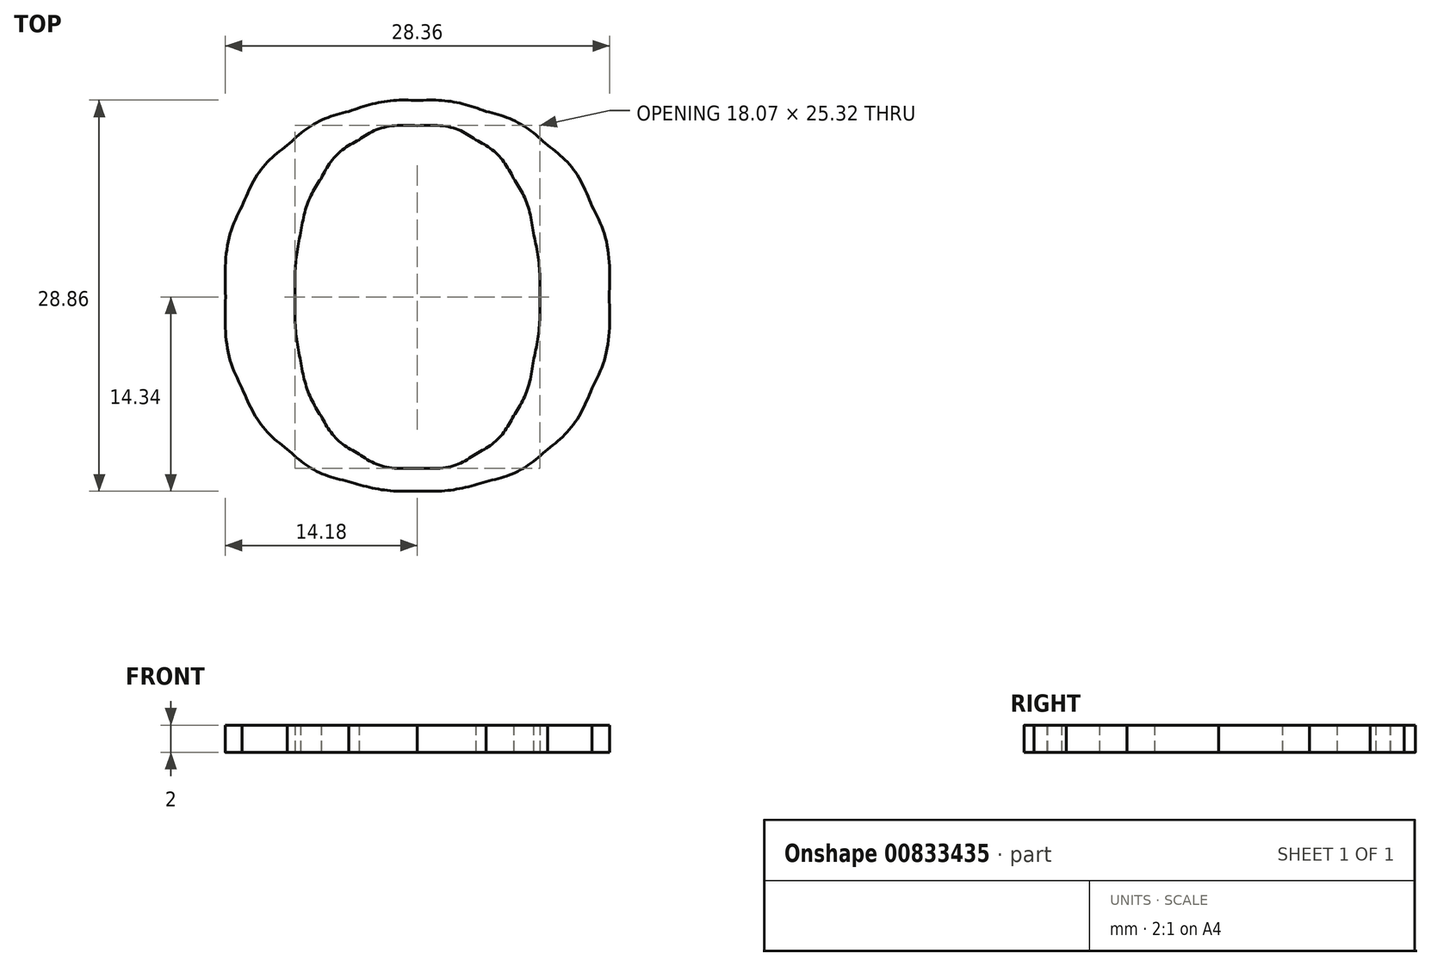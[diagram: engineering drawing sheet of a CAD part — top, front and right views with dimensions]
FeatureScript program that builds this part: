
annotation { "Feature Type Name" : "Feature", "Feature Type Description" : "" }
export const myFeature = defineFeature(function(context is Context, id is Id, definition is map)
    precondition{}
    {
        {
            var Q0;
            Q0=qCreatedBy(makeId("Top.planeOp"),FACE);
            var sketch = newSketch(context, id + "F0", { "sketchPlane" : qUnion([Q0])});
            skLineSegment(sketch, "E0", {"start": v(-37.54, 32.6) * mm, "end": v(-37.54, 22.58) * mm});
            skLineSegment(sketch, "E1", {"start": v(-37.54, 22.58) * mm, "end": v(-37.54, 32.6) * mm});
            skLineSegment(sketch, "E2", {"start": v(-32.77, 18.91) * mm, "end": v(-32.77, 22.4) * mm});
            skLineSegment(sketch, "E3", {"start": v(-32.77, 22.4) * mm, "end": v(-32.77, 24.68) * mm});
            skLineSegment(sketch, "E4", {"start": v(-32.77, 24.68) * mm, "end": v(-32.77, 18.91) * mm});
            skLineSegment(sketch, "E5", {"start": v(-9.25, 34.75) * mm, "end": v(-9.25, 24.21) * mm});
            skLineSegment(sketch, "E6", {"start": v(-9.25, 24.21) * mm, "end": v(-9.25, 34.75) * mm});
            skLineSegment(sketch, "E7", {"start": v(-4.94, 17.7) * mm, "end": v(-4.94, 21.19) * mm});
            skLineSegment(sketch, "E8", {"start": v(-4.94, 21.19) * mm, "end": v(-4.94, 17.7) * mm});
            skLineSegment(sketch, "E9", {"start": v(-4.94, 24.15) * mm, "end": v(-4.94, 34.75) * mm});
            skLineSegment(sketch, "E10", {"start": v(-4.94, 34.75) * mm, "end": v(-4.94, 24.15) * mm});
            skLineSegment(sketch, "E11", {"start": v(-35.72, -38.69) * mm, "end": v(-36.42, -38.69) * mm});
            skLineSegment(sketch, "E12", {"start": v(-36.42, -38.69) * mm, "end": v(-35.72, -38.69) * mm});
            skLineSegment(sketch, "E13", {"start": v(-17.56, -13.13) * mm, "end": v(-16.86, -13.13) * mm});
            skLineSegment(sketch, "E14", {"start": v(-16.86, -13.13) * mm, "end": v(-17.56, -13.13) * mm});
            skLineSegment(sketch, "E15", {"start": v(-7.25, -35.54) * mm, "end": v(-7.25, -44.98) * mm});
            skLineSegment(sketch, "E16", {"start": v(-7.25, -44.98) * mm, "end": v(-7.25, -35.54) * mm});
            skLineSegment(sketch, "E17", {"start": v(-2.94, -44.98) * mm, "end": v(-2.94, -41.3) * mm});
            skLineSegment(sketch, "E18", {"start": v(-2.94, -41.3) * mm, "end": v(-2.83, -41.3) * mm});
            skLineSegment(sketch, "E19", {"start": v(-2.83, -41.3) * mm, "end": v(-2.94, -44.98) * mm});
            skLineSegment(sketch, "E20", {"start": v(-2.83, -24.3) * mm, "end": v(-2.94, -24.3) * mm});
            skLineSegment(sketch, "E21", {"start": v(-2.94, -24.3) * mm, "end": v(-2.83, -24.3) * mm});
            skLineSegment(sketch, "E22", {"start": v(40.76, -31.76) * mm, "end": v(40.53, -40.5) * mm});
            skLineSegment(sketch, "E23", {"start": v(40.53, -40.5) * mm, "end": v(40.76, -31.76) * mm});
            skLineSegment(sketch, "E24", {"start": v(26.38, -21.4) * mm, "end": v(26.38, -24.42) * mm});
            skLineSegment(sketch, "E25", {"start": v(26.38, -24.42) * mm, "end": v(27.02, -24.42) * mm});
            skLineSegment(sketch, "E26", {"start": v(27.02, -24.42) * mm, "end": v(26.38, -21.4) * mm});
            skLineSegment(sketch, "E27", {"start": v(48.45, -45.56) * mm, "end": v(48.45, -44.28) * mm});
            skLineSegment(sketch, "E28", {"start": v(48.45, -44.28) * mm, "end": v(48.45, -45.56) * mm});
            skFitSpline(sketch, "E29", {"points": [v(-37.54, 22.58) * mm, v(-37.54, 20.02) * mm, v(-37.6, 17.5) * mm, v(-37.72, 15.01) * mm]});
            skFitSpline(sketch, "E30", {"points": [v(-37.72, 15.01) * mm, v(-37.8, 12.57) * mm, v(-37.9, 10.1) * mm, v(-38.01, 7.62) * mm]});
            skFitSpline(sketch, "E31", {"points": [v(-38.01, 7.62) * mm, v(-36.23, 7.7) * mm, v(-34.46, 7.74) * mm, v(-32.71, 7.74) * mm]});
            skFitSpline(sketch, "E32", {"points": [v(-32.71, 7.74) * mm, v(-30.97, 7.74) * mm, v(-29.2, 7.74) * mm, v(-27.41, 7.74) * mm]});
            skFitSpline(sketch, "E33", {"points": [v(-27.41, 7.74) * mm, v(-25.63, 7.74) * mm, v(-23.88, 7.74) * mm, v(-22.17, 7.74) * mm]});
            skFitSpline(sketch, "E34", {"points": [v(-22.17, 7.74) * mm, v(-20.43, 7.74) * mm, v(-18.68, 7.7) * mm, v(-16.93, 7.62) * mm]});
            skFitSpline(sketch, "E35", {"points": [v(-16.93, 7.62) * mm, v(-17.05, 8) * mm, v(-17.1, 8.51) * mm, v(-17.1, 9.13) * mm]});
            skFitSpline(sketch, "E36", {"points": [v(-17.1, 9.13) * mm, v(-17.1, 9.4) * mm, v(-17.1, 9.7) * mm, v(-17.1, 10) * mm]});
            skFitSpline(sketch, "E37", {"points": [v(-17.1, 10) * mm, v(-17.07, 10.36) * mm, v(-17.01, 10.67) * mm, v(-16.93, 10.94) * mm]});
            skFitSpline(sketch, "E38", {"points": [v(-16.93, 10.94) * mm, v(-17.87, 10.74) * mm, v(-18.97, 10.59) * mm, v(-20.25, 10.47) * mm]});
            skFitSpline(sketch, "E39", {"points": [v(-20.25, 10.47) * mm, v(-21.5, 10.4) * mm, v(-22.83, 10.32) * mm, v(-24.27, 10.24) * mm]});
            skFitSpline(sketch, "E40", {"points": [v(-24.27, 10.24) * mm, v(-25.67, 10.2) * mm, v(-27.1, 10.18) * mm, v(-28.58, 10.18) * mm]});
            skFitSpline(sketch, "E41", {"points": [v(-28.58, 10.18) * mm, v(-30.01, 10.18) * mm, v(-31.37, 10.18) * mm, v(-32.65, 10.18) * mm]});
            skFitSpline(sketch, "E42", {"points": [v(-32.65, 10.18) * mm, v(-32.7, 10.92) * mm, v(-32.73, 12) * mm, v(-32.77, 13.44) * mm]});
            skFitSpline(sketch, "E43", {"points": [v(-32.77, 13.44) * mm, v(-32.77, 14.88) * mm, v(-32.77, 16.7) * mm, v(-32.77, 18.91) * mm]});
            skFitSpline(sketch, "E44", {"points": [v(-32.77, 24.68) * mm, v(-32.77, 25.3) * mm, v(-32.77, 25.8) * mm, v(-32.77, 26.2) * mm]});
            skFitSpline(sketch, "E45", {"points": [v(-32.77, 26.2) * mm, v(-32.73, 26.62) * mm, v(-32.71, 27) * mm, v(-32.71, 27.36) * mm]});
            skFitSpline(sketch, "E46", {"points": [v(-32.71, 27.36) * mm, v(-32.01, 27.36) * mm, v(-31.08, 27.34) * mm, v(-29.92, 27.3) * mm]});
            skFitSpline(sketch, "E47", {"points": [v(-29.92, 27.3) * mm, v(-28.71, 27.3) * mm, v(-27.45, 27.28) * mm, v(-26.13, 27.24) * mm]});
            skFitSpline(sketch, "E48", {"points": [v(-26.13, 27.24) * mm, v(-24.77, 27.24) * mm, v(-23.44, 27.2) * mm, v(-22.12, 27.12) * mm]});
            skFitSpline(sketch, "E49", {"points": [v(-22.12, 27.12) * mm, v(-20.76, 27.05) * mm, v(-19.57, 26.95) * mm, v(-18.56, 26.83) * mm]});
            skFitSpline(sketch, "E50", {"points": [v(-18.56, 26.83) * mm, v(-18.68, 27.42) * mm, v(-18.74, 28) * mm, v(-18.74, 28.58) * mm]});
            skFitSpline(sketch, "E51", {"points": [v(-18.74, 28.58) * mm, v(-18.74, 29.2) * mm, v(-18.68, 29.8) * mm, v(-18.56, 30.38) * mm]});
            skFitSpline(sketch, "E52", {"points": [v(-18.56, 30.38) * mm, v(-19.42, 30.3) * mm, v(-20.33, 30.23) * mm, v(-21.3, 30.15) * mm]});
            skFitSpline(sketch, "E53", {"points": [v(-21.3, 30.15) * mm, v(-22.23, 30.11) * mm, v(-23.26, 30.06) * mm, v(-24.39, 29.98) * mm]});
            skFitSpline(sketch, "E54", {"points": [v(-24.39, 29.98) * mm, v(-25.51, 29.94) * mm, v(-26.75, 29.9) * mm, v(-28.11, 29.86) * mm]});
            skFitSpline(sketch, "E55", {"points": [v(-28.11, 29.86) * mm, v(-29.47, 29.82) * mm, v(-31, 29.8) * mm, v(-32.71, 29.8) * mm]});
            skFitSpline(sketch, "E56", {"points": [v(-32.71, 29.8) * mm, v(-32.71, 30.54) * mm, v(-32.73, 31.63) * mm, v(-32.77, 33.06) * mm]});
            skFitSpline(sketch, "E57", {"points": [v(-32.77, 33.06) * mm, v(-32.77, 34.5) * mm, v(-32.77, 35.97) * mm, v(-32.77, 37.49) * mm]});
            skFitSpline(sketch, "E58", {"points": [v(-32.77, 37.49) * mm, v(-32.77, 38.92) * mm, v(-32.75, 40.2) * mm, v(-32.71, 41.33) * mm]});
            skFitSpline(sketch, "E59", {"points": [v(-32.71, 41.33) * mm, v(-32.63, 42.46) * mm, v(-32.58, 43.64) * mm, v(-32.54, 44.88) * mm]});
            skFitSpline(sketch, "E60", {"points": [v(-32.54, 44.88) * mm, v(-30.64, 44.88) * mm, v(-29, 44.84) * mm, v(-27.65, 44.77) * mm]});
            skFitSpline(sketch, "E61", {"points": [v(-27.65, 44.77) * mm, v(-26.29, 44.73) * mm, v(-25.05, 44.67) * mm, v(-23.92, 44.6) * mm]});
            skFitSpline(sketch, "E62", {"points": [v(-23.92, 44.6) * mm, v(-22.76, 44.51) * mm, v(-21.67, 44.44) * mm, v(-20.66, 44.36) * mm]});
            skFitSpline(sketch, "E63", {"points": [v(-20.66, 44.36) * mm, v(-19.61, 44.28) * mm, v(-18.47, 44.2) * mm, v(-17.22, 44.13) * mm]});
            skFitSpline(sketch, "E64", {"points": [v(-17.22, 44.13) * mm, v(-17.34, 44.7) * mm, v(-17.4, 45.3) * mm, v(-17.4, 45.87) * mm]});
            skFitSpline(sketch, "E65", {"points": [v(-17.4, 45.87) * mm, v(-17.4, 46.45) * mm, v(-17.34, 47.04) * mm, v(-17.22, 47.62) * mm]});
            skFitSpline(sketch, "E66", {"points": [v(-17.22, 47.62) * mm, v(-18.97, 47.54) * mm, v(-20.7, 47.46) * mm, v(-22.4, 47.39) * mm]});
            skFitSpline(sketch, "E67", {"points": [v(-22.4, 47.39) * mm, v(-24.11, 47.35) * mm, v(-25.84, 47.33) * mm, v(-27.59, 47.33) * mm]});
            skFitSpline(sketch, "E68", {"points": [v(-27.59, 47.33) * mm, v(-29.34, 47.33) * mm, v(-31.08, 47.35) * mm, v(-32.83, 47.39) * mm]});
            skFitSpline(sketch, "E69", {"points": [v(-32.83, 47.39) * mm, v(-34.54, 47.46) * mm, v(-36.26, 47.54) * mm, v(-38.01, 47.62) * mm]});
            skFitSpline(sketch, "E70", {"points": [v(-38.01, 47.62) * mm, v(-37.9, 45.14) * mm, v(-37.8, 42.65) * mm, v(-37.72, 40.17) * mm]});
            skFitSpline(sketch, "E71", {"points": [v(-37.72, 40.17) * mm, v(-37.6, 37.68) * mm, v(-37.54, 35.16) * mm, v(-37.54, 32.6) * mm]});
            skFitSpline(sketch, "E72", {"points": [v(-9.25, 24.21) * mm, v(-9.25, 22.9) * mm, v(-9.27, 21.46) * mm, v(-9.3, 19.9) * mm]});
            skFitSpline(sketch, "E73", {"points": [v(-9.3, 19.9) * mm, v(-9.3, 18.35) * mm, v(-9.33, 16.82) * mm, v(-9.36, 15.3) * mm]});
            skFitSpline(sketch, "E74", {"points": [v(-9.36, 15.3) * mm, v(-9.4, 13.8) * mm, v(-9.46, 12.35) * mm, v(-9.54, 11) * mm]});
            skFitSpline(sketch, "E75", {"points": [v(-9.54, 11) * mm, v(-9.58, 9.64) * mm, v(-9.64, 8.51) * mm, v(-9.71, 7.62) * mm]});
            skFitSpline(sketch, "E76", {"points": [v(-9.71, 7.62) * mm, v(-8.82, 7.7) * mm, v(-7.95, 7.74) * mm, v(-7.1, 7.74) * mm]});
            skFitSpline(sketch, "E77", {"points": [v(-7.1, 7.74) * mm, v(-6.24, 7.74) * mm, v(-5.37, 7.7) * mm, v(-4.47, 7.62) * mm]});
            skFitSpline(sketch, "E78", {"points": [v(-4.47, 7.62) * mm, v(-4.67, 9.29) * mm, v(-4.8, 10.94) * mm, v(-4.88, 12.57) * mm]});
            skFitSpline(sketch, "E79", {"points": [v(-4.88, 12.57) * mm, v(-4.92, 14.24) * mm, v(-4.94, 15.95) * mm, v(-4.94, 17.7) * mm]});
            skFitSpline(sketch, "E80", {"points": [v(-4.94, 21.19) * mm, v(-4.94, 21.65) * mm, v(-4.75, 21.88) * mm, v(-4.36, 21.88) * mm]});
            skFitSpline(sketch, "E81", {"points": [v(-4.36, 21.88) * mm, v(-4.2, 21.88) * mm, v(-4.05, 21.83) * mm, v(-3.9, 21.7) * mm]});
            skFitSpline(sketch, "E82", {"points": [v(-3.9, 21.7) * mm, v(-3.74, 21.6) * mm, v(-3.6, 21.46) * mm, v(-3.48, 21.3) * mm]});
            skFitSpline(sketch, "E83", {"points": [v(-3.48, 21.3) * mm, v(-2.79, 20.56) * mm, v(-1.95, 19.63) * mm, v(-0.98, 18.5) * mm]});
            skFitSpline(sketch, "E84", {"points": [v(-0.98, 18.5) * mm, v(0, 17.38) * mm, v(1, 16.18) * mm, v(2.05, 14.9) * mm]});
            skFitSpline(sketch, "E85", {"points": [v(2.05, 14.9) * mm, v(3.13, 13.62) * mm, v(4.22, 12.32) * mm, v(5.3, 11) * mm]});
            skFitSpline(sketch, "E86", {"points": [v(5.3, 11) * mm, v(6.4, 9.72) * mm, v(7.37, 8.59) * mm, v(8.22, 7.62) * mm]});
            skFitSpline(sketch, "E87", {"points": [v(8.22, 7.62) * mm, v(8.76, 7.7) * mm, v(9.29, 7.74) * mm, v(9.8, 7.74) * mm]});
            skFitSpline(sketch, "E88", {"points": [v(9.8, 7.74) * mm, v(10.3, 7.74) * mm, v(10.76, 7.74) * mm, v(11.19, 7.74) * mm]});
            skFitSpline(sketch, "E89", {"points": [v(11.19, 7.74) * mm, v(11.7, 7.74) * mm, v(12.2, 7.74) * mm, v(12.7, 7.74) * mm]});
            skFitSpline(sketch, "E90", {"points": [v(12.7, 7.74) * mm, v(13.25, 7.74) * mm, v(13.85, 7.7) * mm, v(14.5, 7.62) * mm]});
            skFitSpline(sketch, "E91", {"points": [v(14.5, 7.62) * mm, v(12.06, 10.22) * mm, v(9.66, 12.86) * mm, v(7.29, 15.54) * mm]});
            skFitSpline(sketch, "E92", {"points": [v(7.29, 15.54) * mm, v(4.96, 18.22) * mm, v(2.69, 20.9) * mm, v(0.48, 23.57) * mm]});
            skFitSpline(sketch, "E93", {"points": [v(0.48, 23.57) * mm, v(2.5, 25.55) * mm, v(4.6, 27.5) * mm, v(6.82, 29.4) * mm]});
            skFitSpline(sketch, "E94", {"points": [v(6.82, 29.4) * mm, v(9.07, 31.34) * mm, v(11.42, 33.3) * mm, v(13.87, 35.28) * mm]});
            skFitSpline(sketch, "E95", {"points": [v(13.87, 35.28) * mm, v(13.2, 35.2) * mm, v(12.66, 35.12) * mm, v(12.24, 35.04) * mm]});
            skFitSpline(sketch, "E96", {"points": [v(12.24, 35.04) * mm, v(11.8, 35) * mm, v(11.38, 34.98) * mm, v(10.96, 34.98) * mm]});
            skFitSpline(sketch, "E97", {"points": [v(10.96, 34.98) * mm, v(10.26, 34.98) * mm, v(9.52, 35.08) * mm, v(8.74, 35.28) * mm]});
            skFitSpline(sketch, "E98", {"points": [v(8.74, 35.28) * mm, v(7.85, 34.23) * mm, v(6.86, 33.12) * mm, v(5.77, 31.96) * mm]});
            skFitSpline(sketch, "E99", {"points": [v(5.77, 31.96) * mm, v(4.69, 30.8) * mm, v(3.62, 29.69) * mm, v(2.57, 28.64) * mm]});
            skFitSpline(sketch, "E100", {"points": [v(2.57, 28.64) * mm, v(1.56, 27.63) * mm, v(0.63, 26.74) * mm, v(-0.22, 25.96) * mm]});
            skFitSpline(sketch, "E101", {"points": [v(-0.22, 25.96) * mm, v(-1.04, 25.18) * mm, v(-1.62, 24.66) * mm, v(-1.97, 24.39) * mm]});
            skFitSpline(sketch, "E102", {"points": [v(-1.97, 24.39) * mm, v(-2.44, 24.04) * mm, v(-2.86, 23.73) * mm, v(-3.25, 23.46) * mm]});
            skFitSpline(sketch, "E103", {"points": [v(-3.25, 23.46) * mm, v(-3.6, 23.18) * mm, v(-3.93, 23.05) * mm, v(-4.24, 23.05) * mm]});
            skFitSpline(sketch, "E104", {"points": [v(-4.24, 23.05) * mm, v(-4.7, 23.05) * mm, v(-4.94, 23.42) * mm, v(-4.94, 24.15) * mm]});
            skFitSpline(sketch, "E105", {"points": [v(-4.94, 34.75) * mm, v(-4.94, 36.07) * mm, v(-4.94, 37.5) * mm, v(-4.94, 39.06) * mm]});
            skFitSpline(sketch, "E106", {"points": [v(-4.94, 39.06) * mm, v(-4.9, 40.61) * mm, v(-4.86, 42.15) * mm, v(-4.82, 43.66) * mm]});
            skFitSpline(sketch, "E107", {"points": [v(-4.82, 43.66) * mm, v(-4.78, 45.17) * mm, v(-4.75, 46.61) * mm, v(-4.7, 47.97) * mm]});
            skFitSpline(sketch, "E108", {"points": [v(-4.7, 47.97) * mm, v(-4.63, 49.37) * mm, v(-4.55, 50.55) * mm, v(-4.47, 51.52) * mm]});
            skFitSpline(sketch, "E109", {"points": [v(-4.47, 51.52) * mm, v(-5.56, 51.33) * mm, v(-6.43, 51.23) * mm, v(-7.1, 51.23) * mm]});
            skFitSpline(sketch, "E110", {"points": [v(-7.1, 51.23) * mm, v(-7.75, 51.23) * mm, v(-8.63, 51.33) * mm, v(-9.71, 51.52) * mm]});
            skFitSpline(sketch, "E111", {"points": [v(-9.71, 51.52) * mm, v(-9.64, 50.55) * mm, v(-9.58, 49.37) * mm, v(-9.54, 47.97) * mm]});
            skFitSpline(sketch, "E112", {"points": [v(-9.54, 47.97) * mm, v(-9.46, 46.61) * mm, v(-9.4, 45.17) * mm, v(-9.36, 43.66) * mm]});
            skFitSpline(sketch, "E113", {"points": [v(-9.36, 43.66) * mm, v(-9.33, 42.15) * mm, v(-9.3, 40.61) * mm, v(-9.3, 39.06) * mm]});
            skFitSpline(sketch, "E114", {"points": [v(-9.3, 39.06) * mm, v(-9.27, 37.5) * mm, v(-9.25, 36.07) * mm, v(-9.25, 34.75) * mm]});
            skFitSpline(sketch, "E115", {"points": [v(22.13, 21.36) * mm, v(22.13, 23) * mm, v(22.27, 24.56) * mm, v(22.54, 26.08) * mm]});
            skFitSpline(sketch, "E116", {"points": [v(22.54, 26.08) * mm, v(22.85, 27.6) * mm, v(23.36, 28.93) * mm, v(24.06, 30.1) * mm]});
            skFitSpline(sketch, "E117", {"points": [v(24.06, 30.1) * mm, v(24.75, 31.3) * mm, v(25.69, 32.25) * mm, v(26.85, 32.95) * mm]});
            skFitSpline(sketch, "E118", {"points": [v(26.85, 32.95) * mm, v(28.02, 33.65) * mm, v(29.45, 34) * mm, v(31.16, 34) * mm]});
            skFitSpline(sketch, "E119", {"points": [v(31.16, 34) * mm, v(32.87, 34) * mm, v(34.3, 33.65) * mm, v(35.47, 32.95) * mm]});
            skFitSpline(sketch, "E120", {"points": [v(35.47, 32.95) * mm, v(36.63, 32.25) * mm, v(37.56, 31.3) * mm, v(38.26, 30.1) * mm]});
            skFitSpline(sketch, "E121", {"points": [v(38.26, 30.1) * mm, v(38.96, 28.93) * mm, v(39.45, 27.6) * mm, v(39.72, 26.08) * mm]});
            skFitSpline(sketch, "E122", {"points": [v(39.72, 26.08) * mm, v(40.03, 24.56) * mm, v(40.18, 23) * mm, v(40.18, 21.36) * mm]});
            skFitSpline(sketch, "E123", {"points": [v(40.18, 21.36) * mm, v(40.18, 19.73) * mm, v(40.03, 18.16) * mm, v(39.72, 16.64) * mm]});
            skFitSpline(sketch, "E124", {"points": [v(39.72, 16.64) * mm, v(39.45, 15.13) * mm, v(38.96, 13.77) * mm, v(38.26, 12.57) * mm]});
            skFitSpline(sketch, "E125", {"points": [v(38.26, 12.57) * mm, v(37.56, 11.4) * mm, v(36.63, 10.47) * mm, v(35.47, 9.77) * mm]});
            skFitSpline(sketch, "E126", {"points": [v(35.47, 9.77) * mm, v(34.3, 9.07) * mm, v(32.87, 8.73) * mm, v(31.16, 8.73) * mm]});
            skFitSpline(sketch, "E127", {"points": [v(31.16, 8.73) * mm, v(29.45, 8.73) * mm, v(28.02, 9.07) * mm, v(26.85, 9.77) * mm]});
            skFitSpline(sketch, "E128", {"points": [v(26.85, 9.77) * mm, v(25.69, 10.47) * mm, v(24.75, 11.4) * mm, v(24.06, 12.57) * mm]});
            skFitSpline(sketch, "E129", {"points": [v(24.06, 12.57) * mm, v(23.36, 13.77) * mm, v(22.85, 15.13) * mm, v(22.54, 16.64) * mm]});
            skFitSpline(sketch, "E130", {"points": [v(22.54, 16.64) * mm, v(22.27, 18.16) * mm, v(22.13, 19.73) * mm, v(22.13, 21.36) * mm]});
            skFitSpline(sketch, "E131", {"points": [v(17.01, 21.36) * mm, v(17.01, 18.72) * mm, v(17.42, 16.47) * mm, v(18.23, 14.6) * mm]});
            skFitSpline(sketch, "E132", {"points": [v(18.23, 14.6) * mm, v(19.09, 12.78) * mm, v(20.2, 11.29) * mm, v(21.55, 10.12) * mm]});
            skFitSpline(sketch, "E133", {"points": [v(21.55, 10.12) * mm, v(22.91, 9) * mm, v(24.43, 8.2) * mm, v(26.1, 7.74) * mm]});
            skFitSpline(sketch, "E134", {"points": [v(26.1, 7.74) * mm, v(27.8, 7.27) * mm, v(29.5, 7.04) * mm, v(31.16, 7.04) * mm]});
            skFitSpline(sketch, "E135", {"points": [v(31.16, 7.04) * mm, v(32.87, 7.04) * mm, v(34.56, 7.27) * mm, v(36.23, 7.74) * mm]});
            skFitSpline(sketch, "E136", {"points": [v(36.23, 7.74) * mm, v(37.9, 8.2) * mm, v(39.4, 9) * mm, v(40.77, 10.12) * mm]});
            skFitSpline(sketch, "E137", {"points": [v(40.77, 10.12) * mm, v(42.13, 11.29) * mm, v(43.21, 12.78) * mm, v(44.03, 14.6) * mm]});
            skFitSpline(sketch, "E138", {"points": [v(44.03, 14.6) * mm, v(44.88, 16.47) * mm, v(45.3, 18.72) * mm, v(45.3, 21.36) * mm]});
            skFitSpline(sketch, "E139", {"points": [v(45.3, 21.36) * mm, v(45.3, 24) * mm, v(44.88, 26.23) * mm, v(44.03, 28.06) * mm]});
            skFitSpline(sketch, "E140", {"points": [v(44.03, 28.06) * mm, v(43.21, 29.92) * mm, v(42.13, 31.41) * mm, v(40.77, 32.54) * mm]});
            skFitSpline(sketch, "E141", {"points": [v(40.77, 32.54) * mm, v(39.4, 33.7) * mm, v(37.9, 34.54) * mm, v(36.23, 35.04) * mm]});
            skFitSpline(sketch, "E142", {"points": [v(36.23, 35.04) * mm, v(34.56, 35.59) * mm, v(32.87, 35.86) * mm, v(31.16, 35.86) * mm]});
            skFitSpline(sketch, "E143", {"points": [v(31.16, 35.86) * mm, v(29.5, 35.86) * mm, v(27.8, 35.59) * mm, v(26.1, 35.04) * mm]});
            skFitSpline(sketch, "E144", {"points": [v(26.1, 35.04) * mm, v(24.43, 34.54) * mm, v(22.91, 33.7) * mm, v(21.55, 32.54) * mm]});
            skFitSpline(sketch, "E145", {"points": [v(21.55, 32.54) * mm, v(20.2, 31.41) * mm, v(19.09, 29.92) * mm, v(18.23, 28.06) * mm]});
            skFitSpline(sketch, "E146", {"points": [v(18.23, 28.06) * mm, v(17.42, 26.23) * mm, v(17.01, 24) * mm, v(17.01, 21.36) * mm]});
            skFitSpline(sketch, "E147", {"points": [v(-36.42, -38.69) * mm, v(-36.54, -39.81) * mm, v(-36.67, -40.75) * mm, v(-36.83, -41.48) * mm]});
            skFitSpline(sketch, "E148", {"points": [v(-36.83, -41.48) * mm, v(-36.95, -42.18) * mm, v(-37.18, -42.98) * mm, v(-37.53, -43.87) * mm]});
            skFitSpline(sketch, "E149", {"points": [v(-37.53, -43.87) * mm, v(-36.52, -44.69) * mm, v(-35.28, -45.42) * mm, v(-33.8, -46.08) * mm]});
            skFitSpline(sketch, "E150", {"points": [v(-33.8, -46.08) * mm, v(-32.29, -46.7) * mm, v(-30.33, -47.01) * mm, v(-27.92, -47.01) * mm]});
            skFitSpline(sketch, "E151", {"points": [v(-27.92, -47.01) * mm, v(-25.67, -47.01) * mm, v(-23.67, -46.7) * mm, v(-21.92, -46.08) * mm]});
            skFitSpline(sketch, "E152", {"points": [v(-21.92, -46.08) * mm, v(-20.14, -45.42) * mm, v(-18.64, -44.51) * mm, v(-17.44, -43.35) * mm]});
            skFitSpline(sketch, "E153", {"points": [v(-17.44, -43.35) * mm, v(-16.2, -42.14) * mm, v(-15.27, -40.75) * mm, v(-14.65, -39.15) * mm]});
            skFitSpline(sketch, "E154", {"points": [v(-14.65, -39.15) * mm, v(-13.99, -37.56) * mm, v(-13.66, -35.87) * mm, v(-13.66, -34.09) * mm]});
            skFitSpline(sketch, "E155", {"points": [v(-13.66, -34.09) * mm, v(-13.66, -31.95) * mm, v(-14.12, -30.25) * mm, v(-15.05, -28.97) * mm]});
            skFitSpline(sketch, "E156", {"points": [v(-15.05, -28.97) * mm, v(-15.95, -27.68) * mm, v(-17.07, -26.64) * mm, v(-18.43, -25.82) * mm]});
            skFitSpline(sketch, "E157", {"points": [v(-18.43, -25.82) * mm, v(-19.79, -25) * mm, v(-21.26, -24.33) * mm, v(-22.86, -23.78) * mm]});
            skFitSpline(sketch, "E158", {"points": [v(-22.86, -23.78) * mm, v(-24.4, -23.2) * mm, v(-25.86, -22.56) * mm, v(-27.22, -21.86) * mm]});
            skFitSpline(sketch, "E159", {"points": [v(-27.22, -21.86) * mm, v(-28.58, -21.12) * mm, v(-29.73, -20.23) * mm, v(-30.66, -19.18) * mm]});
            skFitSpline(sketch, "E160", {"points": [v(-30.66, -19.18) * mm, v(-31.55, -18.14) * mm, v(-32, -16.7) * mm, v(-32, -14.88) * mm]});
            skFitSpline(sketch, "E161", {"points": [v(-32, -14.88) * mm, v(-32, -13.83) * mm, v(-31.82, -12.86) * mm, v(-31.47, -11.96) * mm]});
            skFitSpline(sketch, "E162", {"points": [v(-31.47, -11.96) * mm, v(-31.08, -11.07) * mm, v(-30.56, -10.31) * mm, v(-29.9, -9.7) * mm]});
            skFitSpline(sketch, "E163", {"points": [v(-29.9, -9.7) * mm, v(-29.2, -9.03) * mm, v(-28.4, -8.53) * mm, v(-27.51, -8.18) * mm]});
            skFitSpline(sketch, "E164", {"points": [v(-27.51, -8.18) * mm, v(-26.58, -7.83) * mm, v(-25.57, -7.66) * mm, v(-24.49, -7.66) * mm]});
            skFitSpline(sketch, "E165", {"points": [v(-24.49, -7.66) * mm, v(-23.4, -7.66) * mm, v(-22.47, -7.85) * mm, v(-21.7, -8.24) * mm]});
            skFitSpline(sketch, "E166", {"points": [v(-21.7, -8.24) * mm, v(-20.91, -8.59) * mm, v(-20.25, -9.03) * mm, v(-19.71, -9.58) * mm]});
            skFitSpline(sketch, "E167", {"points": [v(-19.71, -9.58) * mm, v(-19.13, -10.12) * mm, v(-18.68, -10.72) * mm, v(-18.37, -11.38) * mm]});
            skFitSpline(sketch, "E168", {"points": [v(-18.37, -11.38) * mm, v(-18.02, -12) * mm, v(-17.75, -12.59) * mm, v(-17.56, -13.13) * mm]});
            skFitSpline(sketch, "E169", {"points": [v(-16.86, -13.13) * mm, v(-16.63, -12) * mm, v(-16.4, -11.07) * mm, v(-16.16, -10.33) * mm]});
            skFitSpline(sketch, "E170", {"points": [v(-16.16, -10.33) * mm, v(-15.93, -9.6) * mm, v(-15.64, -8.9) * mm, v(-15.29, -8.24) * mm]});
            skFitSpline(sketch, "E171", {"points": [v(-15.29, -8.24) * mm, v(-16.45, -7.3) * mm, v(-17.71, -6.63) * mm, v(-19.07, -6.2) * mm]});
            skFitSpline(sketch, "E172", {"points": [v(-19.07, -6.2) * mm, v(-20.43, -5.73) * mm, v(-22.04, -5.5) * mm, v(-23.9, -5.5) * mm]});
            skFitSpline(sketch, "E173", {"points": [v(-23.9, -5.5) * mm, v(-25.84, -5.5) * mm, v(-27.6, -5.77) * mm, v(-29.14, -6.32) * mm]});
            skFitSpline(sketch, "E174", {"points": [v(-29.14, -6.32) * mm, v(-30.7, -6.86) * mm, v(-32.04, -7.62) * mm, v(-33.16, -8.59) * mm]});
            skFitSpline(sketch, "E175", {"points": [v(-33.16, -8.59) * mm, v(-34.25, -9.56) * mm, v(-35.08, -10.72) * mm, v(-35.66, -12.08) * mm]});
            skFitSpline(sketch, "E176", {"points": [v(-35.66, -12.08) * mm, v(-36.25, -13.4) * mm, v(-36.54, -14.88) * mm, v(-36.54, -16.5) * mm]});
            skFitSpline(sketch, "E177", {"points": [v(-36.54, -16.5) * mm, v(-36.54, -18.8) * mm, v(-36.1, -20.62) * mm, v(-35.2, -21.98) * mm]});
            skFitSpline(sketch, "E178", {"points": [v(-35.2, -21.98) * mm, v(-34.27, -23.34) * mm, v(-33.12, -24.46) * mm, v(-31.76, -25.36) * mm]});
            skFitSpline(sketch, "E179", {"points": [v(-31.76, -25.36) * mm, v(-30.4, -26.2) * mm, v(-28.95, -26.93) * mm, v(-27.4, -27.5) * mm]});
            skFitSpline(sketch, "E180", {"points": [v(-27.4, -27.5) * mm, v(-25.8, -28.1) * mm, v(-24.33, -28.73) * mm, v(-22.97, -29.43) * mm]});
            skFitSpline(sketch, "E181", {"points": [v(-22.97, -29.43) * mm, v(-21.61, -30.13) * mm, v(-20.49, -31) * mm, v(-19.6, -32.05) * mm]});
            skFitSpline(sketch, "E182", {"points": [v(-19.6, -32.05) * mm, v(-18.66, -33.1) * mm, v(-18.2, -34.52) * mm, v(-18.2, -36.3) * mm]});
            skFitSpline(sketch, "E183", {"points": [v(-18.2, -36.3) * mm, v(-18.2, -37.47) * mm, v(-18.4, -38.57) * mm, v(-18.78, -39.62) * mm]});
            skFitSpline(sketch, "E184", {"points": [v(-18.78, -39.62) * mm, v(-19.17, -40.63) * mm, v(-19.73, -41.52) * mm, v(-20.47, -42.3) * mm]});
            skFitSpline(sketch, "E185", {"points": [v(-20.47, -42.3) * mm, v(-21.17, -43.04) * mm, v(-22.04, -43.64) * mm, v(-23.09, -44.1) * mm]});
            skFitSpline(sketch, "E186", {"points": [v(-23.09, -44.1) * mm, v(-24.1, -44.53) * mm, v(-25.24, -44.74) * mm, v(-26.52, -44.74) * mm]});
            skFitSpline(sketch, "E187", {"points": [v(-26.52, -44.74) * mm, v(-27.77, -44.74) * mm, v(-28.9, -44.57) * mm, v(-29.9, -44.22) * mm]});
            skFitSpline(sketch, "E188", {"points": [v(-29.9, -44.22) * mm, v(-30.9, -43.83) * mm, v(-31.8, -43.35) * mm, v(-32.58, -42.76) * mm]});
            skFitSpline(sketch, "E189", {"points": [v(-32.58, -42.76) * mm, v(-33.32, -42.18) * mm, v(-33.96, -41.54) * mm, v(-34.5, -40.84) * mm]});
            skFitSpline(sketch, "E190", {"points": [v(-34.5, -40.84) * mm, v(-35, -40.1) * mm, v(-35.41, -39.39) * mm, v(-35.72, -38.69) * mm]});
            skFitSpline(sketch, "E191", {"points": [v(-7.25, -44.98) * mm, v(-7.25, -46.22) * mm, v(-7.27, -47.6) * mm, v(-7.3, -49.11) * mm]});
            skFitSpline(sketch, "E192", {"points": [v(-7.3, -49.11) * mm, v(-7.3, -50.66) * mm, v(-7.33, -52.2) * mm, v(-7.37, -53.71) * mm]});
            skFitSpline(sketch, "E193", {"points": [v(-7.37, -53.71) * mm, v(-7.4, -55.22) * mm, v(-7.46, -56.66) * mm, v(-7.54, -58.02) * mm]});
            skFitSpline(sketch, "E194", {"points": [v(-7.54, -58.02) * mm, v(-7.58, -59.42) * mm, v(-7.64, -60.6) * mm, v(-7.72, -61.57) * mm]});
            skFitSpline(sketch, "E195", {"points": [v(-7.72, -61.57) * mm, v(-6.63, -61.38) * mm, v(-5.76, -61.28) * mm, v(-5.1, -61.28) * mm]});
            skFitSpline(sketch, "E196", {"points": [v(-5.1, -61.28) * mm, v(-4.44, -61.28) * mm, v(-3.56, -61.38) * mm, v(-2.48, -61.57) * mm]});
            skFitSpline(sketch, "E197", {"points": [v(-2.48, -61.57) * mm, v(-2.55, -60.6) * mm, v(-2.63, -59.42) * mm, v(-2.7, -58.02) * mm]});
            skFitSpline(sketch, "E198", {"points": [v(-2.7, -58.02) * mm, v(-2.75, -56.66) * mm, v(-2.79, -55.22) * mm, v(-2.83, -53.71) * mm]});
            skFitSpline(sketch, "E199", {"points": [v(-2.83, -53.71) * mm, v(-2.87, -52.2) * mm, v(-2.9, -50.66) * mm, v(-2.94, -49.11) * mm]});
            skFitSpline(sketch, "E200", {"points": [v(-2.94, -49.11) * mm, v(-2.94, -47.6) * mm, v(-2.94, -46.22) * mm, v(-2.94, -44.98) * mm]});
            skFitSpline(sketch, "E201", {"points": [v(-2.83, -41.3) * mm, v(-1, -45) * mm, v(2.05, -46.84) * mm, v(6.31, -46.84) * mm]});
            skFitSpline(sketch, "E202", {"points": [v(6.31, -46.84) * mm, v(7.83, -46.84) * mm, v(9.34, -46.57) * mm, v(10.86, -46.03) * mm]});
            skFitSpline(sketch, "E203", {"points": [v(10.86, -46.03) * mm, v(12.37, -45.44) * mm, v(13.7, -44.55) * mm, v(14.87, -43.35) * mm]});
            skFitSpline(sketch, "E204", {"points": [v(14.87, -43.35) * mm, v(16.08, -42.14) * mm, v(17.05, -40.63) * mm, v(17.78, -38.8) * mm]});
            skFitSpline(sketch, "E205", {"points": [v(17.78, -38.8) * mm, v(18.52, -36.98) * mm, v(18.9, -34.83) * mm, v(18.9, -32.34) * mm]});
            skFitSpline(sketch, "E206", {"points": [v(18.9, -32.34) * mm, v(18.9, -29.86) * mm, v(18.54, -27.72) * mm, v(17.84, -25.94) * mm]});
            skFitSpline(sketch, "E207", {"points": [v(17.84, -25.94) * mm, v(17.18, -24.11) * mm, v(16.3, -22.62) * mm, v(15.16, -21.45) * mm]});
            skFitSpline(sketch, "E208", {"points": [v(15.16, -21.45) * mm, v(14.08, -20.3) * mm, v(12.82, -19.44) * mm, v(11.38, -18.9) * mm]});
            skFitSpline(sketch, "E209", {"points": [v(11.38, -18.9) * mm, v(9.94, -18.31) * mm, v(8.49, -18.02) * mm, v(7.01, -18.02) * mm]});
            skFitSpline(sketch, "E210", {"points": [v(7.01, -18.02) * mm, v(5.58, -18.02) * mm, v(4.3, -18.23) * mm, v(3.17, -18.66) * mm]});
            skFitSpline(sketch, "E211", {"points": [v(3.17, -18.66) * mm, v(2.05, -19.09) * mm, v(1.07, -19.63) * mm, v(0.26, -20.3) * mm]});
            skFitSpline(sketch, "E212", {"points": [v(0.26, -20.3) * mm, v(-0.52, -20.91) * mm, v(-1.16, -21.6) * mm, v(-1.66, -22.33) * mm]});
            skFitSpline(sketch, "E213", {"points": [v(-1.66, -22.33) * mm, v(-2.17, -23.03) * mm, v(-2.55, -23.69) * mm, v(-2.83, -24.3) * mm]});
            skFitSpline(sketch, "E214", {"points": [v(-2.94, -24.3) * mm, v(-2.94, -23.38) * mm, v(-2.9, -22.44) * mm, v(-2.83, -21.51) * mm]});
            skFitSpline(sketch, "E215", {"points": [v(-2.83, -21.51) * mm, v(-2.75, -20.58) * mm, v(-2.63, -19.61) * mm, v(-2.48, -18.6) * mm]});
            skFitSpline(sketch, "E216", {"points": [v(-2.48, -18.6) * mm, v(-3.56, -18.8) * mm, v(-4.44, -18.9) * mm, v(-5.1, -18.9) * mm]});
            skFitSpline(sketch, "E217", {"points": [v(-5.1, -18.9) * mm, v(-5.76, -18.9) * mm, v(-6.63, -18.8) * mm, v(-7.72, -18.6) * mm]});
            skFitSpline(sketch, "E218", {"points": [v(-7.72, -18.6) * mm, v(-7.64, -19.61) * mm, v(-7.58, -20.81) * mm, v(-7.54, -22.21) * mm]});
            skFitSpline(sketch, "E219", {"points": [v(-7.54, -22.21) * mm, v(-7.46, -23.6) * mm, v(-7.4, -25.08) * mm, v(-7.37, -26.64) * mm]});
            skFitSpline(sketch, "E220", {"points": [v(-7.37, -26.64) * mm, v(-7.33, -28.15) * mm, v(-7.3, -29.68) * mm, v(-7.3, -31.24) * mm]});
            skFitSpline(sketch, "E221", {"points": [v(-7.3, -31.24) * mm, v(-7.27, -32.79) * mm, v(-7.25, -34.23) * mm, v(-7.25, -35.54) * mm]});
            skFitSpline(sketch, "E222", {"points": [v(13.77, -32.28) * mm, v(13.77, -34.03) * mm, v(13.6, -35.68) * mm, v(13.24, -37.23) * mm]});
            skFitSpline(sketch, "E223", {"points": [v(13.24, -37.23) * mm, v(12.93, -38.75) * mm, v(12.43, -40.09) * mm, v(11.73, -41.25) * mm]});
            skFitSpline(sketch, "E224", {"points": [v(11.73, -41.25) * mm, v(11.07, -42.38) * mm, v(10.22, -43.27) * mm, v(9.17, -43.93) * mm]});
            skFitSpline(sketch, "E225", {"points": [v(9.17, -43.93) * mm, v(8.16, -44.55) * mm, v(6.96, -44.86) * mm, v(5.56, -44.86) * mm]});
            skFitSpline(sketch, "E226", {"points": [v(5.56, -44.86) * mm, v(-0.1, -44.86) * mm, v(-2.94, -40.82) * mm, v(-2.94, -32.75) * mm]});
            skFitSpline(sketch, "E227", {"points": [v(-2.94, -32.75) * mm, v(-2.94, -31.08) * mm, v(-2.79, -29.5) * mm, v(-2.48, -28.03) * mm]});
            skFitSpline(sketch, "E228", {"points": [v(-2.48, -28.03) * mm, v(-2.17, -26.52) * mm, v(-1.66, -25.22) * mm, v(-0.96, -24.13) * mm]});
            skFitSpline(sketch, "E229", {"points": [v(-0.96, -24.13) * mm, v(-0.26, -23) * mm, v(0.63, -22.11) * mm, v(1.72, -21.45) * mm]});
            skFitSpline(sketch, "E230", {"points": [v(1.72, -21.45) * mm, v(2.84, -20.8) * mm, v(4.18, -20.46) * mm, v(5.73, -20.46) * mm]});
            skFitSpline(sketch, "E231", {"points": [v(5.73, -20.46) * mm, v(6.66, -20.46) * mm, v(7.62, -20.64) * mm, v(8.59, -20.99) * mm]});
            skFitSpline(sketch, "E232", {"points": [v(8.59, -20.99) * mm, v(9.56, -21.34) * mm, v(10.4, -21.98) * mm, v(11.15, -22.91) * mm]});
            skFitSpline(sketch, "E233", {"points": [v(11.15, -22.91) * mm, v(11.92, -23.8) * mm, v(12.54, -25) * mm, v(13.01, -26.52) * mm]});
            skFitSpline(sketch, "E234", {"points": [v(13.01, -26.52) * mm, v(13.52, -28.03) * mm, v(13.77, -29.96) * mm, v(13.77, -32.28) * mm]});
            skFitSpline(sketch, "E235", {"points": [v(40.53, -40.5) * mm, v(39.87, -41.58) * mm, v(38.92, -42.53) * mm, v(37.68, -43.35) * mm]});
            skFitSpline(sketch, "E236", {"points": [v(37.68, -43.35) * mm, v(36.47, -44.16) * mm, v(35.13, -44.57) * mm, v(33.66, -44.57) * mm]});
            skFitSpline(sketch, "E237", {"points": [v(33.66, -44.57) * mm, v(32.38, -44.57) * mm, v(31.21, -44.1) * mm, v(30.17, -43.17) * mm]});
            skFitSpline(sketch, "E238", {"points": [v(30.17, -43.17) * mm, v(29.12, -42.24) * mm, v(28.6, -40.86) * mm, v(28.6, -39.04) * mm]});
            skFitSpline(sketch, "E239", {"points": [v(28.6, -39.04) * mm, v(28.6, -37.95) * mm, v(28.79, -37.06) * mm, v(29.18, -36.36) * mm]});
            skFitSpline(sketch, "E240", {"points": [v(29.18, -36.36) * mm, v(29.6, -35.66) * mm, v(30.15, -35.08) * mm, v(30.8, -34.61) * mm]});
            skFitSpline(sketch, "E241", {"points": [v(30.8, -34.61) * mm, v(31.5, -34.15) * mm, v(32.28, -33.78) * mm, v(33.14, -33.5) * mm]});
            skFitSpline(sketch, "E242", {"points": [v(33.14, -33.5) * mm, v(34.03, -33.24) * mm, v(34.92, -33.02) * mm, v(35.81, -32.87) * mm]});
            skFitSpline(sketch, "E243", {"points": [v(35.81, -32.87) * mm, v(36.7, -32.67) * mm, v(37.58, -32.5) * mm, v(38.43, -32.34) * mm]});
            skFitSpline(sketch, "E244", {"points": [v(38.43, -32.34) * mm, v(39.33, -32.19) * mm, v(40.1, -32) * mm, v(40.76, -31.76) * mm]});
            skFitSpline(sketch, "E245", {"points": [v(27.02, -24.42) * mm, v(27.68, -23.18) * mm, v(28.67, -22.21) * mm, v(30, -21.51) * mm]});
            skFitSpline(sketch, "E246", {"points": [v(30, -21.51) * mm, v(31.35, -20.81) * mm, v(32.8, -20.46) * mm, v(34.36, -20.46) * mm]});
            skFitSpline(sketch, "E247", {"points": [v(34.36, -20.46) * mm, v(35.52, -20.46) * mm, v(36.51, -20.68) * mm, v(37.33, -21.1) * mm]});
            skFitSpline(sketch, "E248", {"points": [v(37.33, -21.1) * mm, v(38.14, -21.5) * mm, v(38.8, -22.02) * mm, v(39.3, -22.68) * mm]});
            skFitSpline(sketch, "E249", {"points": [v(39.3, -22.68) * mm, v(39.81, -23.34) * mm, v(40.18, -24.11) * mm, v(40.41, -25) * mm]});
            skFitSpline(sketch, "E250", {"points": [v(40.41, -25) * mm, v(40.65, -25.9) * mm, v(40.76, -26.83) * mm, v(40.76, -27.8) * mm]});
            skFitSpline(sketch, "E251", {"points": [v(40.76, -27.8) * mm, v(40.76, -28.38) * mm, v(40.7, -28.87) * mm, v(40.59, -29.26) * mm]});
            skFitSpline(sketch, "E252", {"points": [v(40.59, -29.26) * mm, v(40.47, -29.6) * mm, v(40.12, -29.92) * mm, v(39.54, -30.19) * mm]});
            skFitSpline(sketch, "E253", {"points": [v(39.54, -30.19) * mm, v(39, -30.46) * mm, v(38.12, -30.73) * mm, v(36.92, -31) * mm]});
            skFitSpline(sketch, "E254", {"points": [v(36.92, -31) * mm, v(35.76, -31.24) * mm, v(34.13, -31.53) * mm, v(32.03, -31.88) * mm]});
            skFitSpline(sketch, "E255", {"points": [v(32.03, -31.88) * mm, v(29.47, -32.3) * mm, v(27.45, -33.16) * mm, v(25.97, -34.44) * mm]});
            skFitSpline(sketch, "E256", {"points": [v(25.97, -34.44) * mm, v(24.54, -35.72) * mm, v(23.82, -37.52) * mm, v(23.82, -39.85) * mm]});
            skFitSpline(sketch, "E257", {"points": [v(23.82, -39.85) * mm, v(23.82, -40.98) * mm, v(24.03, -41.99) * mm, v(24.46, -42.88) * mm]});
            skFitSpline(sketch, "E258", {"points": [v(24.46, -42.88) * mm, v(24.93, -43.73) * mm, v(25.5, -44.47) * mm, v(26.2, -45.1) * mm]});
            skFitSpline(sketch, "E259", {"points": [v(26.2, -45.1) * mm, v(26.94, -45.71) * mm, v(27.78, -46.16) * mm, v(28.71, -46.43) * mm]});
            skFitSpline(sketch, "E260", {"points": [v(28.71, -46.43) * mm, v(29.64, -46.7) * mm, v(30.6, -46.84) * mm, v(31.56, -46.84) * mm]});
            skFitSpline(sketch, "E261", {"points": [v(31.56, -46.84) * mm, v(33.54, -46.84) * mm, v(35.21, -46.51) * mm, v(36.57, -45.85) * mm]});
            skFitSpline(sketch, "E262", {"points": [v(36.57, -45.85) * mm, v(37.93, -45.2) * mm, v(39.3, -44.16) * mm, v(40.7, -42.76) * mm]});
            skFitSpline(sketch, "E263", {"points": [v(40.7, -42.76) * mm, v(40.82, -43.77) * mm, v(41.2, -44.6) * mm, v(41.87, -45.27) * mm]});
            skFitSpline(sketch, "E264", {"points": [v(41.87, -45.27) * mm, v(42.53, -45.89) * mm, v(43.48, -46.2) * mm, v(44.72, -46.2) * mm]});
            skFitSpline(sketch, "E265", {"points": [v(44.72, -46.2) * mm, v(45.5, -46.2) * mm, v(46.2, -46.14) * mm, v(46.82, -46.03) * mm]});
            skFitSpline(sketch, "E266", {"points": [v(46.82, -46.03) * mm, v(47.48, -45.9) * mm, v(48.02, -45.75) * mm, v(48.45, -45.56) * mm]});
            skFitSpline(sketch, "E267", {"points": [v(48.45, -44.28) * mm, v(48.25, -44.4) * mm, v(48.04, -44.47) * mm, v(47.8, -44.51) * mm]});
            skFitSpline(sketch, "E268", {"points": [v(47.8, -44.51) * mm, v(47.61, -44.51) * mm, v(47.42, -44.51) * mm, v(47.23, -44.51) * mm]});
            skFitSpline(sketch, "E269", {"points": [v(47.23, -44.51) * mm, v(46.64, -44.51) * mm, v(46.2, -44.38) * mm, v(45.89, -44.1) * mm]});
            skFitSpline(sketch, "E270", {"points": [v(45.89, -44.1) * mm, v(45.61, -43.83) * mm, v(45.4, -43.5) * mm, v(45.25, -43.11) * mm]});
            skFitSpline(sketch, "E271", {"points": [v(45.25, -43.11) * mm, v(45.1, -42.69) * mm, v(45, -42.22) * mm, v(44.95, -41.72) * mm]});
            skFitSpline(sketch, "E272", {"points": [v(44.95, -41.72) * mm, v(44.95, -41.17) * mm, v(44.95, -40.67) * mm, v(44.95, -40.2) * mm]});
            skFitSpline(sketch, "E273", {"points": [v(44.95, -40.2) * mm, v(44.95, -37.76) * mm, v(45, -35.45) * mm, v(45.07, -33.27) * mm]});
            skFitSpline(sketch, "E274", {"points": [v(45.07, -33.27) * mm, v(45.15, -31.06) * mm, v(45.19, -28.85) * mm, v(45.19, -26.64) * mm]});
            skFitSpline(sketch, "E275", {"points": [v(45.19, -26.64) * mm, v(45.19, -25.36) * mm, v(44.95, -24.2) * mm, v(44.49, -23.14) * mm]});
            skFitSpline(sketch, "E276", {"points": [v(44.49, -23.14) * mm, v(44.02, -22.06) * mm, v(43.38, -21.14) * mm, v(42.57, -20.4) * mm]});
            skFitSpline(sketch, "E277", {"points": [v(42.57, -20.4) * mm, v(41.75, -19.63) * mm, v(40.76, -19.05) * mm, v(39.6, -18.66) * mm]});
            skFitSpline(sketch, "E278", {"points": [v(39.6, -18.66) * mm, v(38.43, -18.23) * mm, v(37.15, -18.02) * mm, v(35.76, -18.02) * mm]});
            skFitSpline(sketch, "E279", {"points": [v(35.76, -18.02) * mm, v(34.2, -18.02) * mm, v(32.69, -18.25) * mm, v(31.21, -18.72) * mm]});
            skFitSpline(sketch, "E280", {"points": [v(31.21, -18.72) * mm, v(29.74, -19.18) * mm, v(28.13, -20.08) * mm, v(26.38, -21.4) * mm]});
            skSolve(sketch);
        }
        {
            var Q0;
            Q0=makeQuery(id+"F0.imprint","IMPRINT",FACE,{"disambiguationData":[TD([[makeQuery(id+"F0.imprint","IMPRINT",EDGE,{"derivedFrom":sQuery(id+"F0.wireOp",EDGE,"E1")}),-1.0]])]});
            var Q1;
            Q1=makeQuery(id+"F0.imprint","IMPRINT",FACE,{"disambiguationData":[TD([[makeQuery(id+"F0.imprint","IMPRINT",EDGE,{"derivedFrom":sQuery(id+"F0.wireOp",EDGE,"E6")}),-1.0]])]});
            var Q2;
            Q2=makeQuery(id+"F0.imprint","IMPRINT",FACE,{"disambiguationData":[TD([[makeQuery(id+"F0.imprint","IMPRINT",EDGE,{"derivedFrom":sQuery(id+"F0.wireOp",EDGE,"E115")}),1.0]])]});
            var Q3;
            Q3=makeQuery(id+"F0.imprint","IMPRINT",FACE,{"disambiguationData":[TD([[makeQuery(id+"F0.imprint","IMPRINT",EDGE,{"derivedFrom":sQuery(id+"F0.wireOp",EDGE,"E12")}),-1.0]])]});
            var Q4;
            Q4=makeQuery(id+"F0.imprint","IMPRINT",FACE,{"disambiguationData":[TD([[makeQuery(id+"F0.imprint","IMPRINT",EDGE,{"derivedFrom":sQuery(id+"F0.wireOp",EDGE,"E16")}),-1.0]])]});
            var Q5;
            Q5=makeQuery(id+"F0.imprint","IMPRINT",FACE,{"disambiguationData":[TD([[makeQuery(id+"F0.imprint","IMPRINT",EDGE,{"derivedFrom":sQuery(id+"F0.wireOp",EDGE,"E23")}),-1.0]])]});
            extrude(context, id + "F1", {"entities" : qUnion([Q0, Q1, Q2, Q3, Q4, Q5]), "depth" : 2 * mm, "offsetDistance" : 25 * mm});
        }
    });
